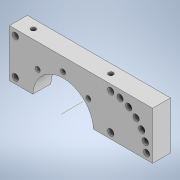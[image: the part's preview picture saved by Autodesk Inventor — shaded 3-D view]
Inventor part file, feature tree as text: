
AUTODESK INVENTOR PART (.ipt)
format: ipt  version: 2020 (Build 240168000, 168)  size: 173,056 bytes
history: native  units: in
note: dims shown in document units (in); Inventor stores cm internally (conversion verified against a paired STEP export)
features: extrude x5, sketch x4, other x1
ambient origin geometry x8: Origin, YZ Plane, XZ Plane, XY Plane, X Axis, Y Axis, Z Axis, Center Point
bodies: Solid1 (feature_tree)
feature tree (10):
  extrude  "Extrusion1"  Depth=6.0in
  extrude  "Extrusion2"  Depth=0.75in
  other  "Work Axis1"
  extrude  "Extrusion3"  TaperAngle=0.0deg  [1 undecoded]
  extrude  "Extrusion4"  Depth=2.0in
  extrude  "Extrusion5"  Depth=0.3937in
  sketch  "Sketch1"  dims[d0=2.0in d1=6.0in]
  sketch  "Sketch2"  dims[d2=0.75in d3=0.0in d15=0.05in]
  sketch  "Sketch3"  dims[d16=2.54in d17=0.0in d18=0.0in]
  sketch  "Sketch5"  dims[d19=0.201in d20=0.375in d22=0.7874in d24=3.25in d25=0.3937in d27=1.0in d29=0.0in d30=0.0in d31=0.2031in d32=1.5in d34=1.1811in d36=90.0deg d38=0.0in d39=0.0in d40=2.25in d41=1.625in d42=45.0deg d43=0.2656in d44=2.0in d45=0.25in d53=0.7874in d55=1.5in d56=0.7874in d58=4.0in d61=2.7559in d63=90.0deg d65=0.0in d66=0.0in]
note: 1 required parameter value undecoded (feature->parameter linkage not recoverable at this tier; creation-order binding heuristic only, values carry confidence <= 0.55)
